# Revit family: NBS_CordekLtd_DschrgeAndVntltngStackTrmntns_GroundLevelVentBox-CGV-020
name_source: partatom
category: Specialty Equipment
revit_build: Autodesk Revit 2014 (Build: 20131024_2115(x64)
units: mm (PartAtom-declared; Revit-internal decimal feet)

## types (1)
- CGV-020
    Arrangement = Ground level vent box with slotted lid
    AssetType = Fixed
    BIMObjectName = NBS_CordekLtd_DischargeAndVentilatingStackTerminations_GroundLevelVentBox-CGV-020
    Category = Pr_65_52_61_23:Discharge and ventilating stack terminations
    ConnectionSizes = Gas inlet: 110 mm; Water outlet: 110 mm
    Description = Ground level vent box with galvanized steel slotted lid
    DurationUnit = year
    Features = Side connection into vent box prevents surface water from entering the gas inlet, base connection to stormwater collection, land drainage or soakaway system, removable mesh over drain outlet to prevent blockage by debris
    FreeAirFlow = 19200 mm²
    Height = 275 mm
    IfcExportAs = IfcStackTerminalType
    IfcExportType = NOTDEFINED
    Length = 500 mm
    ManufacturerName = Cordek Ltd
    ManufacturerURL = www.cordek.com
    Material = Lid: Galvanized steel
    ModelNumber = CGV-020
    ModelReference = Ground Level Vent Box - CGV-020
    NBSCertification = http://www.nationalbimlibrary.com
    NBSDescription = Discharge and ventilating stack terminations
    NBSReference = 90-10-60/437
    Name = DischargeAndVentilatingStackTerminations_GroundLevelVentBox-CGV-020_CordekLtd
    NominalHeight = 275 mm
    NominalLength = 500 mm
    NominalWidth = 150 mm
    ProductInformation = www.cordek.com/uploads/data_sheets/M-DS32_ground_level_vent_box_data_sheet_v2_cordek.pdf
    Shape = Rectangular
    Size = 500 x 150 x 275 mm
    Uniclass2 = 90-62-24/422
    Uniclass2015Description = Discharge and ventilating stack terminations
    Uniclass2015Reference = Pr_65_52_61_23
    Uniclass2015Version = Products v1.1
    VentBoxLidMaterial = NBS_Concept_Slotted
    VentBoxMaterial = NBS_Concept
    Version = 1
    WarrantyDurationUnit = year
    Width = 150 mm

## geometry (parser evidence)
native form markers: Sweep x1
no freeform markers — native parametric forms only
